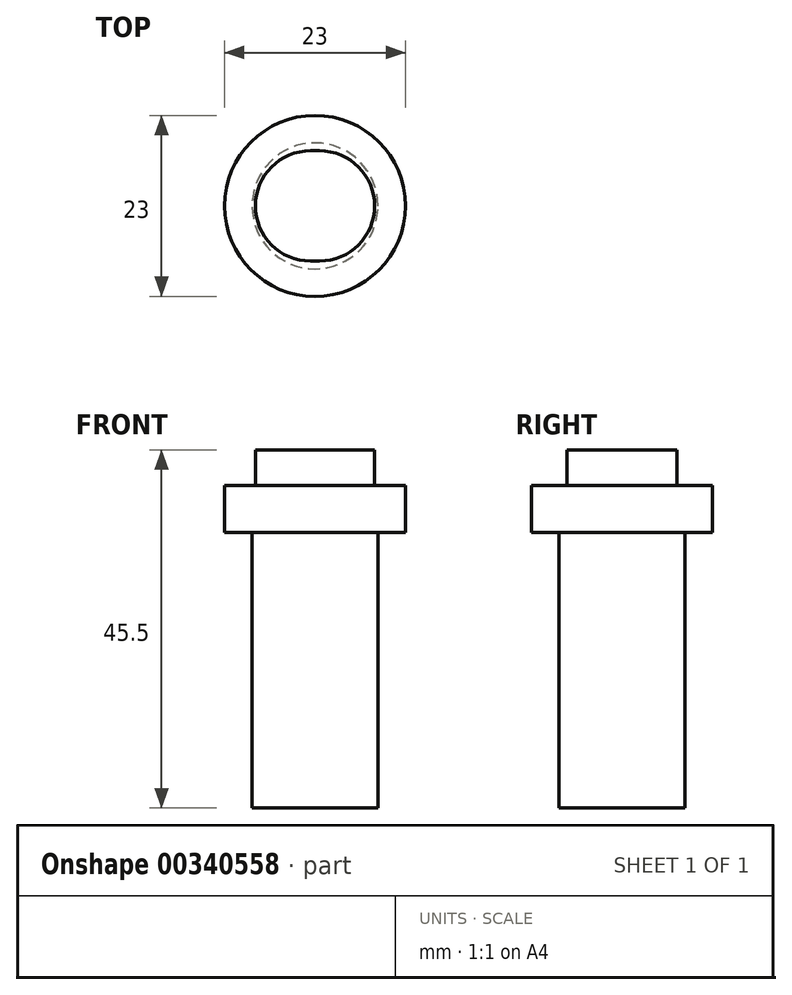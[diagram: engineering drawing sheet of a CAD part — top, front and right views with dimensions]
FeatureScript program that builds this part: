
annotation { "Feature Type Name" : "Feature", "Feature Type Description" : "" }
export const myFeature = defineFeature(function(context is Context, id is Id, definition is map)
    precondition{}
    {
        {
            var Q0;
            Q0=qCreatedBy(makeId("Top.planeOp"),FACE);
            var sketch = newSketch(context, id + "F0", { "sketchPlane" : qUnion([Q0])});
            skCircle(sketch, "E0", {"center": v(0, 0) * mm, "radius": 11.5 * mm});
            skSolve(sketch);
        }
        {
            var Q0;
            Q0 = qSketchRegion(id + "F0", true);
            extrude(context, id + "F1", {"entities" : qUnion([Q0]), "depth" : 10.5 * mm});
        }
        {
            var Q0;
            Q0=makeQuery(id+"F1.opExtrude","CAP_FACE",FACE,{"disambiguationData":[OSD([sQuery(id+"F0.wireOp",EDGE,"E0")])],"isStart":true});
            var sketch = newSketch(context, id + "F2", { "sketchPlane" : qUnion([Q0])});
            skCircle(sketch, "E1", {"center": v(0, 0) * mm, "radius": 8 * mm});
            skSolve(sketch);
        }
        {
            var Q0;
            Q0=makeQuery(id+"F2.imprint","IMPRINT",FACE,{"disambiguationData":[TD([[makeQuery(id+"F2.imprint","IMPRINT",EDGE,{"derivedFrom":sQuery(id+"F2.wireOp",EDGE,"E1")}),1.0]])]});
            extrude(context, id + "F3", {"entities" : qUnion([Q0]), "operationType" : NewBodyOperationType.ADD, "depth" : 35 * mm});
        }
        {
            var Q0;
            Q0=makeQuery(id+"F1.opExtrude","CAP_FACE",FACE,{"disambiguationData":[OSD([sQuery(id+"F0.wireOp",EDGE,"E0")])],"isStart":false});
            var sketch = newSketch(context, id + "F4", { "sketchPlane" : qUnion([Q0])});
            skPoint(sketch, "E2.center.orphan", {"position": v(0, 0) * mm});
            skLineSegment(sketch, "E3", {"start": v(0, 0) * mm, "end": v(0.57, 0) * mm});
            skLineSegment(sketch, "E4", {"start": v(0, 0) * mm, "end": v(-0.57, 0) * mm});
            skArc(sketch, "E5", {"start": v(0.58, -7) * mm, "mid": v(7.58, 0) * mm, "end": v(0.58, 7) * mm});
            skArc(sketch, "E6", {"start": v(-0.57, 7) * mm, "mid": v(-7.58, 0) * mm, "end": v(-0.58, -7) * mm});
            skLineSegment(sketch, "E7", {"start": v(-0.57, -7) * mm, "end": v(0.57, -7) * mm});
            skLineSegment(sketch, "E8", {"start": v(-0.57, 7) * mm, "end": v(0.57, 7) * mm});
            skSolve(sketch);
        }
        {
            var Q0;
            Q0=makeQuery(id+"F4.imprint","IMPRINT",FACE,{"disambiguationData":[TD([[makeQuery(id+"F4.imprint","IMPRINT",EDGE,{"derivedFrom":sQuery(id+"F4.wireOp",EDGE,"E5")}),-1.0]])]});
            extrude(context, id + "F5", {"entities" : qUnion([Q0]), "operationType" : NewBodyOperationType.REMOVE, "oppositeDirection" : true, "depth" : 4.5 * mm});
        }
    });
